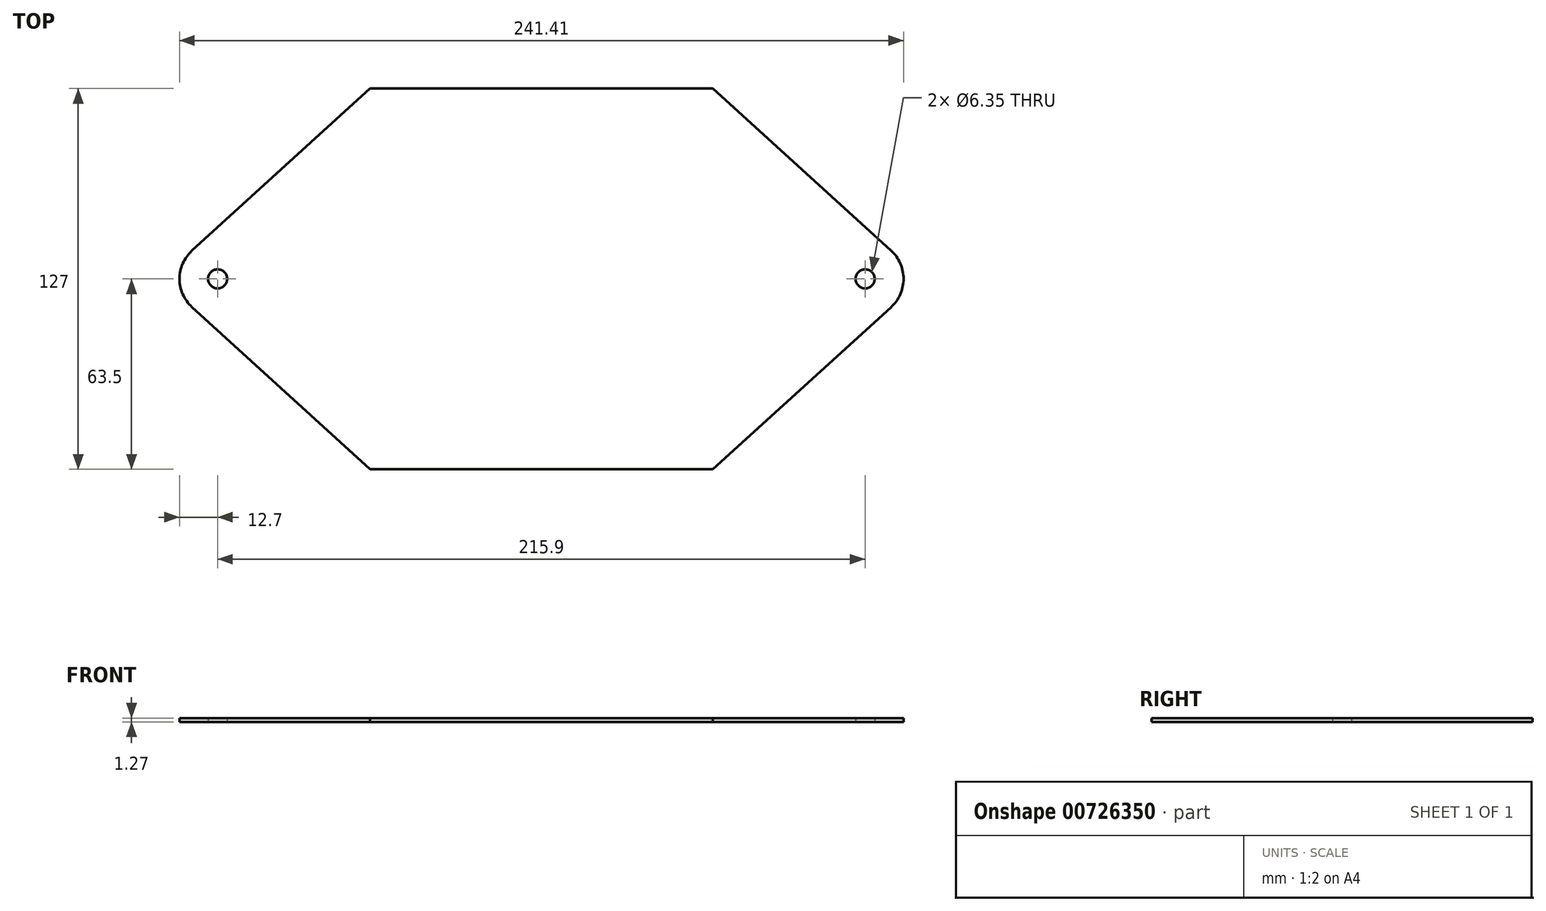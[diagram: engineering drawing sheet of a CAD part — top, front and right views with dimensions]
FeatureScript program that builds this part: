
annotation { "Feature Type Name" : "Feature", "Feature Type Description" : "" }
export const myFeature = defineFeature(function(context is Context, id is Id, definition is map)
    precondition{}
    {
        {
            var Q0;
            Q0=qCreatedBy(makeId("Top.planeOp"),FACE);
            var sketch = newSketch(context, id + "F0", { "sketchPlane" : qUnion([Q0])});
            skLineSegment(sketch, "E0.bottom", {"start": v(57.15, -63.5) * mm, "end": v(-57.15, -63.5) * mm});
            skLineSegment(sketch, "E0.top", {"start": v(57.15, 63.5) * mm, "end": v(-57.15, 63.5) * mm});
            skLineSegment(sketch, "E0.left", {"start": v(57.15, -63.5) * mm, "end": v(57.15, 63.5) * mm});
            skLineSegment(sketch, "E0.right", {"start": v(-57.15, -63.5) * mm, "end": v(-57.15, 63.5) * mm});
            skLineSegment(sketch, "E1", {"start": v(-123.76, 0) * mm, "end": v(106.73, 0) * mm, "construction": true});
            skCircle(sketch, "E2", {"center": v(-107.95, 0) * mm, "radius": 12.7 * mm});
            skCircle(sketch, "E3", {"center": v(107.95, 0) * mm, "radius": 12.8 * mm});
            skCircle(sketch, "E4", {"center": v(-107.95, 0) * mm, "radius": 3.18 * mm});
            skCircle(sketch, "E5", {"center": v(107.95, 0) * mm, "radius": 3.18 * mm});
            skLineSegment(sketch, "E6", {"start": v(-57.15, 63.5) * mm, "end": v(-116.5, 9.39) * mm});
            skLineSegment(sketch, "E7", {"start": v(-57.15, -63.5) * mm, "end": v(-116.5, -9.39) * mm});
            skLineSegment(sketch, "E8", {"start": v(57.15, 63.5) * mm, "end": v(116.57, 9.48) * mm});
            skLineSegment(sketch, "E9", {"start": v(57.15, -63.5) * mm, "end": v(116.57, -9.48) * mm});
            skSolve(sketch);
        }
        {
            var Q0;
            Q0=makeQuery(id+"F0.imprint","IMPRINT",FACE,{"disambiguationData":[TD([[makeQuery(id+"F0.imprint","IMPRINT",EDGE,{"derivedFrom":sQuery(id+"F0.wireOp",EDGE,"E0.right")}),1.0]])]});
            var Q1;
            Q1=makeQuery(id+"F0.imprint","IMPRINT",FACE,{"disambiguationData":[TD([[makeQuery(id+"F0.imprint","IMPRINT",EDGE,{"derivedFrom":sQuery(id+"F0.wireOp",EDGE,"E4")}),-1.0]])]});
            var Q2;
            Q2=makeQuery(id+"F0.imprint","IMPRINT",FACE,{"disambiguationData":[TD([[makeQuery(id+"F0.imprint","IMPRINT",EDGE,{"derivedFrom":sQuery(id+"F0.wireOp",EDGE,"E0.bottom")}),-1.0]])]});
            var Q3;
            Q3=makeQuery(id+"F0.imprint","IMPRINT",FACE,{"disambiguationData":[TD([[makeQuery(id+"F0.imprint","IMPRINT",EDGE,{"derivedFrom":sQuery(id+"F0.wireOp",EDGE,"E0.left")}),-1.0]])]});
            var Q4;
            Q4=makeQuery(id+"F0.imprint","IMPRINT",FACE,{"disambiguationData":[TD([[makeQuery(id+"F0.imprint","IMPRINT",EDGE,{"derivedFrom":sQuery(id+"F0.wireOp",EDGE,"E5")}),-1.0]])]});
            extrude(context, id + "F1", {"entities" : qUnion([Q0, Q1, Q2, Q3, Q4]), "depth" : 1.27 * mm, "offsetDistance" : 25.4 * mm});
        }
    });
